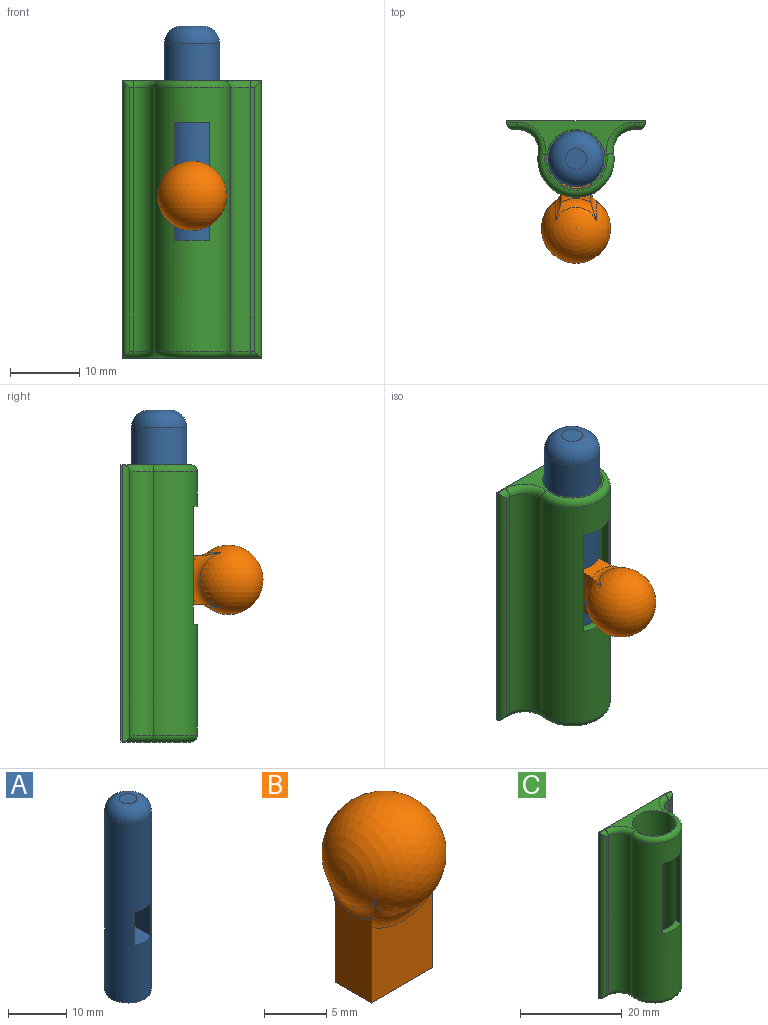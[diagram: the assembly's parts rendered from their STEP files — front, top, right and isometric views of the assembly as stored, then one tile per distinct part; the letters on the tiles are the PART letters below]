
ASSEMBLY  parts=3 mates=2
PART A: 11 faces, bbox 8x8x40 mm
  f0: cylinder r=4mm len=37.5mm, axis (0,0,-1), area 913.2mm2, adj f2,f5,f6,f7,f8,f10
  f1: plane 3x3mm, normal (0,0,1), area 7.1mm2, adj f10
  f2: plane 8x8mm, normal (0,0,-1), area 30.6mm2, adj f0,f3
  f3: cylinder r=2.5mm len=5mm, axis (0,0,-1), area 78.5mm2, adj f2,f4
  f4: plane 5x5mm, normal (0,0,-1), area 19.6mm2, adj f3
  f5: plane 6x4mm, normal (0,0,1), area 23.3mm2, adj f0,f6,f8,f9
  f6: plane 7x5.46mm, normal (-1,0,0), area 38.2mm2, adj f0,f5,f7,f9
  f7: plane 6x4mm, normal (0,0,-1), area 23.3mm2, adj f0,f6,f8,f9
  f8: plane 7x5.46mm, normal (1,0,0), area 38.2mm2, adj f0,f5,f7,f9
  f9: plane 7x4mm, normal (0,-1,0), area 28mm2, adj f5,f6,f7,f8
  f10: torus R=1.5mm, axis (0,0,1), area 76.3mm2, adj f0,f1
PART B: 10 faces, bbox 14.9x11.7x17 mm
  f0: plane 7.49x7mm, normal (0,-1,0), area 46.7mm2, adj f1,f3,f4,f9
  f1: plane 8.25x4.29mm, normal (1,0,0), area 32.2mm2, adj f0,f2,f4,f6,f8,f9
  f2: plane 7.49x7mm, normal (0,1,0), area 46.7mm2, adj f1,f3,f4,f6
  f3: plane 8.25x4.29mm, normal (-1,0,0), area 32.2mm2, adj f0,f2,f4,f6,f7,f9
  f4: plane 7x4.1mm, normal (0,0,-1), area 28.7mm2, adj f0,f1,f2,f3
  f5: sphere r=5mm, area 256.2mm2, adj f6,f7,f8,f9
  f6: torus R=5.71mm, axis (0,1,0), area 15.8mm2, adj f1,f2,f3,f5,f7,f8
  f7: torus R=4.33mm, axis (1,0,0), area 7.3mm2, adj f3,f5,f6,f9
  f8: torus R=4.33mm, axis (1,0,0), area 7.3mm2, adj f1,f5,f6,f9
  f9: torus R=5.71mm, axis (0,1,0), area 15.8mm2, adj f0,f1,f3,f5,f7,f8
PART C: 30 faces, bbox 20x12.4x40 mm
  f0: cylinder r=5.5mm len=38mm, axis (0,0,-1), area 632.5mm2, adj f7,f8,f9,f10,f16,f17,f21,f26
  f1: cylinder r=4.25mm len=35mm, axis (0,0,1), area 843.8mm2, adj f2,f4,f7,f8,f9,f10
  f2: plane 20x10mm, normal (0,0,1), area 32.7mm2, adj f1,f13,f14,f15,f18,f19,f21,f23
  f3: plane 20x10mm, normal (0,0,-1), area 89.4mm2, adj f13,f14,f15,f22,f24,f26,f28,f29
  f4: plane 8.5x8.5mm, normal (0,0,1), area 37.1mm2, adj f1,f5
  f5: cylinder r=2.5mm len=5mm, axis (0,0,1), area 15.7mm2, adj f4,f6
  f6: plane 5x5mm, normal (0,0,1), area 19.6mm2, adj f5
  f7: plane 5x2.06mm, normal (0,0,1), area 6.6mm2, adj f0,f1,f8,f10
  f8: plane 17x1.46mm, normal (-1,0,0), area 24.9mm2, adj f0,f1,f7,f9
  f9: plane 5x2.06mm, normal (0,0,-1), area 6.6mm2, adj f0,f1,f8,f10
  f10: plane 17x1.46mm, normal (1,0,0), area 24.9mm2, adj f0,f1,f7,f9
  f11: plane 38x0.6mm, normal (0,-1,0), area 22.8mm2, adj f16,f25,f27,f29
  f12: plane 38x0.6mm, normal (0,-1,0), area 22.8mm2, adj f17,f18,f20,f22
  f13: plane 40x20mm, normal (0,1,0), area 800mm2, adj f2,f3,f14,f15
  f14: plane 40x0.2mm, normal (1,0,0), area 8mm2, adj f2,f3,f13,f20
  f15: plane 40x0.2mm, normal (-1,0,0), area 8mm2, adj f2,f3,f13,f27
  f16: cylinder r=3mm len=38mm, axis (0,0,-1), area 196.6mm2, adj f0,f11,f23,f28
  f17: cylinder r=3mm len=38mm, axis (0,0,-1), area 196.6mm2, adj f0,f12,f19,f24
  f18: cylinder r=1mm len=1.6mm, axis (1,0,0), area 1.9mm2, adj f2,f12,f19,f20
  f19: torus R=4mm, axis (0,0,1), area 9.1mm2, adj f2,f17,f18,f21
  f20: cylinder r=1mm len=40mm, axis (0,0,1), area 61.7mm2, adj f12,f14,f18,f22
  f21: torus R=4.5mm, axis (0,0,1), area 27.8mm2, adj f0,f2,f19,f23
  f22: cylinder r=1mm len=1.6mm, axis (-1,0,0), area 1.9mm2, adj f3,f12,f20,f24
  f23: torus R=4mm, axis (0,0,1), area 9.1mm2, adj f2,f16,f21,f25
  f24: torus R=4mm, axis (0,0,1), area 9.1mm2, adj f3,f17,f22,f26
  f25: cylinder r=1mm len=1.6mm, axis (1,0,0), area 1.9mm2, adj f2,f11,f23,f27
  f26: torus R=4.5mm, axis (0,0,1), area 27.8mm2, adj f0,f3,f24,f28
  f27: cylinder r=1mm len=40mm, axis (0,0,-1), area 61.7mm2, adj f11,f15,f25,f29
  f28: torus R=4mm, axis (0,0,1), area 9.1mm2, adj f3,f16,f26,f29
  f29: cylinder r=1mm len=1.6mm, axis (-1,0,0), area 1.9mm2, adj f3,f11,f27,f28
PLACE A t=(0,0,7.88)mm
PLACE B rot(axis=(0.58,0.58,-0.58),120deg) t=(0,-5,23.38)mm
PLACE C at identity
MATE fastened A.f9 <-> B.f4  axis (0,-1,0) through (0,2,23.38)mm
MATE slider A.f0 <-> C.f1  axis (0,0,-1) through (0,0,7.88)mm
